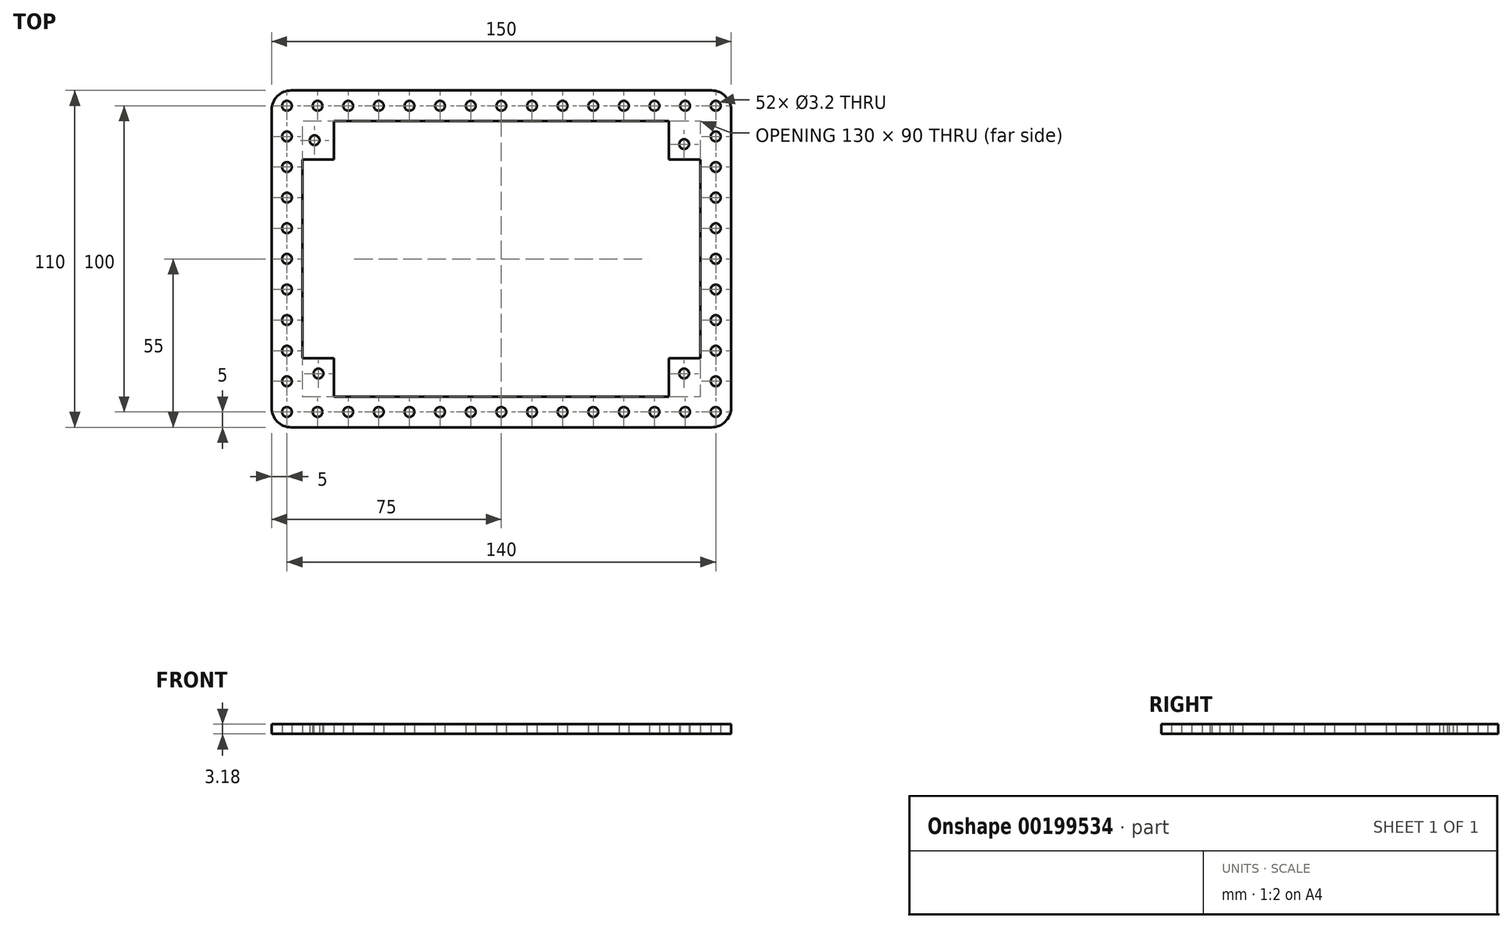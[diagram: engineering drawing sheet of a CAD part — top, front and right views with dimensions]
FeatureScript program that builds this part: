
annotation { "Feature Type Name" : "Feature", "Feature Type Description" : "" }
export const myFeature = defineFeature(function(context is Context, id is Id, definition is map)
    precondition{}
    {
        {
            var Q0;
            Q0=qCreatedBy(makeId("Top.planeOp"),FACE);
            var sketch = newSketch(context, id + "F0", { "sketchPlane" : qUnion([Q0])});
            skLineSegment(sketch, "E0.bottom", {"start": v(6.35, 0) * mm, "end": v(143.65, 0) * mm});
            skLineSegment(sketch, "E0.top", {"start": v(6.35, 110) * mm, "end": v(143.65, 110) * mm});
            skLineSegment(sketch, "E0.left", {"start": v(0, 6.35) * mm, "end": v(0, 103.65) * mm});
            skLineSegment(sketch, "E0.right", {"start": v(150, 6.35) * mm, "end": v(150, 103.65) * mm});
            skPoint(sketch, "E1.visualSharp", {"position": v(0, 110) * mm});
            skArc(sketch, "E1.filletArc", {"start": v(6.35, 110) * mm, "mid": v(1.86, 108.14) * mm, "end": v(0, 103.65) * mm});
            skPoint(sketch, "E2.visualSharp", {"position": v(150, 110) * mm});
            skArc(sketch, "E2.filletArc", {"start": v(150, 103.65) * mm, "mid": v(148.14, 108.14) * mm, "end": v(143.65, 110) * mm});
            skPoint(sketch, "E3.visualSharp", {"position": v(150, 0) * mm});
            skArc(sketch, "E3.filletArc", {"start": v(143.65, 0) * mm, "mid": v(148.14, 1.86) * mm, "end": v(150, 6.35) * mm});
            skPoint(sketch, "E4.visualSharp", {"position": v(0, 0) * mm});
            skArc(sketch, "E4.filletArc", {"start": v(0, 6.35) * mm, "mid": v(1.86, 1.86) * mm, "end": v(6.35, 0) * mm});
            skCircle(sketch, "E5", {"center": v(15.31, 17.54) * mm, "radius": 1.6 * mm});
            skCircle(sketch, "E6", {"center": v(14.04, 93.73) * mm, "radius": 1.6 * mm});
            skCircle(sketch, "E7", {"center": v(134.7, 92.47) * mm, "radius": 1.6 * mm});
            skCircle(sketch, "E8", {"center": v(134.7, 17.54) * mm, "radius": 1.6 * mm});
            skLineSegment(sketch, "E9.bottom", {"start": v(10, 22.54) * mm, "end": v(20.31, 22.54) * mm});
            skLineSegment(sketch, "E9.top", {"start": v(10, 87.47) * mm, "end": v(20.31, 87.47) * mm});
            skLineSegment(sketch, "E9.left", {"start": v(10, 22.54) * mm, "end": v(10, 87.46) * mm});
            skLineSegment(sketch, "E9.right", {"start": v(140, 22.54) * mm, "end": v(140, 87.47) * mm});
            skLineSegment(sketch, "E10.top", {"start": v(20.31, 100) * mm, "end": v(129.7, 100) * mm});
            skLineSegment(sketch, "E10.left", {"start": v(20.31, 87.47) * mm, "end": v(20.31, 100) * mm});
            skLineSegment(sketch, "E10.right", {"start": v(129.7, 87.47) * mm, "end": v(129.7, 100) * mm});
            skLineSegment(sketch, "E11.top", {"start": v(20.31, 10) * mm, "end": v(129.7, 10) * mm});
            skLineSegment(sketch, "E11.left", {"start": v(20.31, 22.54) * mm, "end": v(20.31, 10) * mm});
            skLineSegment(sketch, "E11.right", {"start": v(129.7, 22.54) * mm, "end": v(129.7, 10) * mm});
            skLineSegment(sketch, "E12.trimOffspring", {"start": v(129.7, 22.54) * mm, "end": v(140, 22.54) * mm});
            skLineSegment(sketch, "E13.trimOffspring", {"start": v(129.7, 87.47) * mm, "end": v(140, 87.47) * mm});
            skCircle(sketch, "E14", {"center": v(5, 105) * mm, "radius": 1.6 * mm});
            skCircle(sketch, "E15.1.0.0", {"center": v(15, 105) * mm, "radius": 1.6 * mm});
            skCircle(sketch, "E15.2.0.0", {"center": v(25, 105) * mm, "radius": 1.6 * mm});
            skCircle(sketch, "E15.3.0.0", {"center": v(35, 105) * mm, "radius": 1.6 * mm});
            skCircle(sketch, "E15.4.0.0", {"center": v(45, 105) * mm, "radius": 1.6 * mm});
            skCircle(sketch, "E15.5.0.0", {"center": v(55, 105) * mm, "radius": 1.6 * mm});
            skCircle(sketch, "E15.6.0.0", {"center": v(65, 105) * mm, "radius": 1.6 * mm});
            skCircle(sketch, "E15.7.0.0", {"center": v(75, 105) * mm, "radius": 1.6 * mm});
            skCircle(sketch, "E15.8.0.0", {"center": v(85, 105) * mm, "radius": 1.6 * mm});
            skCircle(sketch, "E15.9.0.0", {"center": v(95, 105) * mm, "radius": 1.6 * mm});
            skCircle(sketch, "E15.10.0.0", {"center": v(105, 105) * mm, "radius": 1.6 * mm});
            skCircle(sketch, "E15.11.0.0", {"center": v(115, 105) * mm, "radius": 1.6 * mm});
            skCircle(sketch, "E15.12.0.0", {"center": v(125, 105) * mm, "radius": 1.6 * mm});
            skCircle(sketch, "E15.13.0.0", {"center": v(135, 105) * mm, "radius": 1.6 * mm});
            skCircle(sketch, "E15.14.0.0", {"center": v(145, 105) * mm, "radius": 1.6 * mm});
            skLineSegment(sketch, "E15.direction1", {"start": v(5, 105) * mm, "end": v(15, 105) * mm, "construction": true});
            skCircle(sketch, "E16.0.1.0", {"center": v(5, 95) * mm, "radius": 1.6 * mm});
            skCircle(sketch, "E16.0.2.0", {"center": v(5, 85) * mm, "radius": 1.6 * mm});
            skCircle(sketch, "E16.0.3.0", {"center": v(5, 75) * mm, "radius": 1.6 * mm});
            skCircle(sketch, "E16.0.4.0", {"center": v(5, 65) * mm, "radius": 1.6 * mm});
            skCircle(sketch, "E16.0.5.0", {"center": v(5, 55) * mm, "radius": 1.6 * mm});
            skCircle(sketch, "E16.0.6.0", {"center": v(5, 45) * mm, "radius": 1.6 * mm});
            skCircle(sketch, "E16.0.7.0", {"center": v(5, 35) * mm, "radius": 1.6 * mm});
            skCircle(sketch, "E16.0.8.0", {"center": v(5, 25) * mm, "radius": 1.6 * mm});
            skCircle(sketch, "E16.0.9.0", {"center": v(5, 15) * mm, "radius": 1.6 * mm});
            skCircle(sketch, "E16.0.10.0", {"center": v(5, 5) * mm, "radius": 1.6 * mm});
            skLineSegment(sketch, "E16.direction1", {"start": v(5, 105) * mm, "end": v(30, 105) * mm, "construction": true});
            skLineSegment(sketch, "E16.direction2", {"start": v(5, 105) * mm, "end": v(5, 95) * mm, "construction": true});
            skCircle(sketch, "E17", {"center": v(145, 5) * mm, "radius": 1.6 * mm});
            skCircle(sketch, "E18.1.0.0", {"center": v(135, 5) * mm, "radius": 1.6 * mm});
            skCircle(sketch, "E18.2.0.0", {"center": v(125, 5) * mm, "radius": 1.6 * mm});
            skCircle(sketch, "E18.3.0.0", {"center": v(115, 5) * mm, "radius": 1.6 * mm});
            skCircle(sketch, "E18.4.0.0", {"center": v(105, 5) * mm, "radius": 1.6 * mm});
            skCircle(sketch, "E18.5.0.0", {"center": v(95, 5) * mm, "radius": 1.6 * mm});
            skCircle(sketch, "E18.6.0.0", {"center": v(85, 5) * mm, "radius": 1.6 * mm});
            skCircle(sketch, "E18.7.0.0", {"center": v(75, 5) * mm, "radius": 1.6 * mm});
            skCircle(sketch, "E18.8.0.0", {"center": v(65, 5) * mm, "radius": 1.6 * mm});
            skCircle(sketch, "E18.9.0.0", {"center": v(55, 5) * mm, "radius": 1.6 * mm});
            skCircle(sketch, "E18.10.0.0", {"center": v(45, 5) * mm, "radius": 1.6 * mm});
            skCircle(sketch, "E18.11.0.0", {"center": v(35, 5) * mm, "radius": 1.6 * mm});
            skCircle(sketch, "E18.12.0.0", {"center": v(25, 5) * mm, "radius": 1.6 * mm});
            skCircle(sketch, "E18.13.0.0", {"center": v(15, 5) * mm, "radius": 1.6 * mm});
            skLineSegment(sketch, "E18.direction1", {"start": v(145, 5) * mm, "end": v(135, 5) * mm, "construction": true});
            skCircle(sketch, "E19.0.1.0", {"center": v(145, 15) * mm, "radius": 1.6 * mm});
            skCircle(sketch, "E19.0.2.0", {"center": v(145, 25) * mm, "radius": 1.6 * mm});
            skCircle(sketch, "E19.0.3.0", {"center": v(145, 35) * mm, "radius": 1.6 * mm});
            skCircle(sketch, "E19.0.4.0", {"center": v(145, 45) * mm, "radius": 1.6 * mm});
            skCircle(sketch, "E19.0.5.0", {"center": v(145, 55) * mm, "radius": 1.6 * mm});
            skCircle(sketch, "E19.0.6.0", {"center": v(145, 65) * mm, "radius": 1.6 * mm});
            skCircle(sketch, "E19.0.7.0", {"center": v(145, 75) * mm, "radius": 1.6 * mm});
            skCircle(sketch, "E19.0.8.0", {"center": v(145, 85) * mm, "radius": 1.6 * mm});
            skCircle(sketch, "E19.0.9.0", {"center": v(145, 95) * mm, "radius": 1.6 * mm});
            skLineSegment(sketch, "E19.direction1", {"start": v(145, 5) * mm, "end": v(170, 5) * mm, "construction": true});
            skLineSegment(sketch, "E19.direction2", {"start": v(145, 5) * mm, "end": v(145, 15) * mm, "construction": true});
            skSolve(sketch);
        }
        {
            var Q0;
            Q0 = qSketchRegion(id + "F0", true);
            extrude(context, id + "F1", {"entities" : qUnion([Q0]), "depth" : 3.17 * mm});
        }
    });
